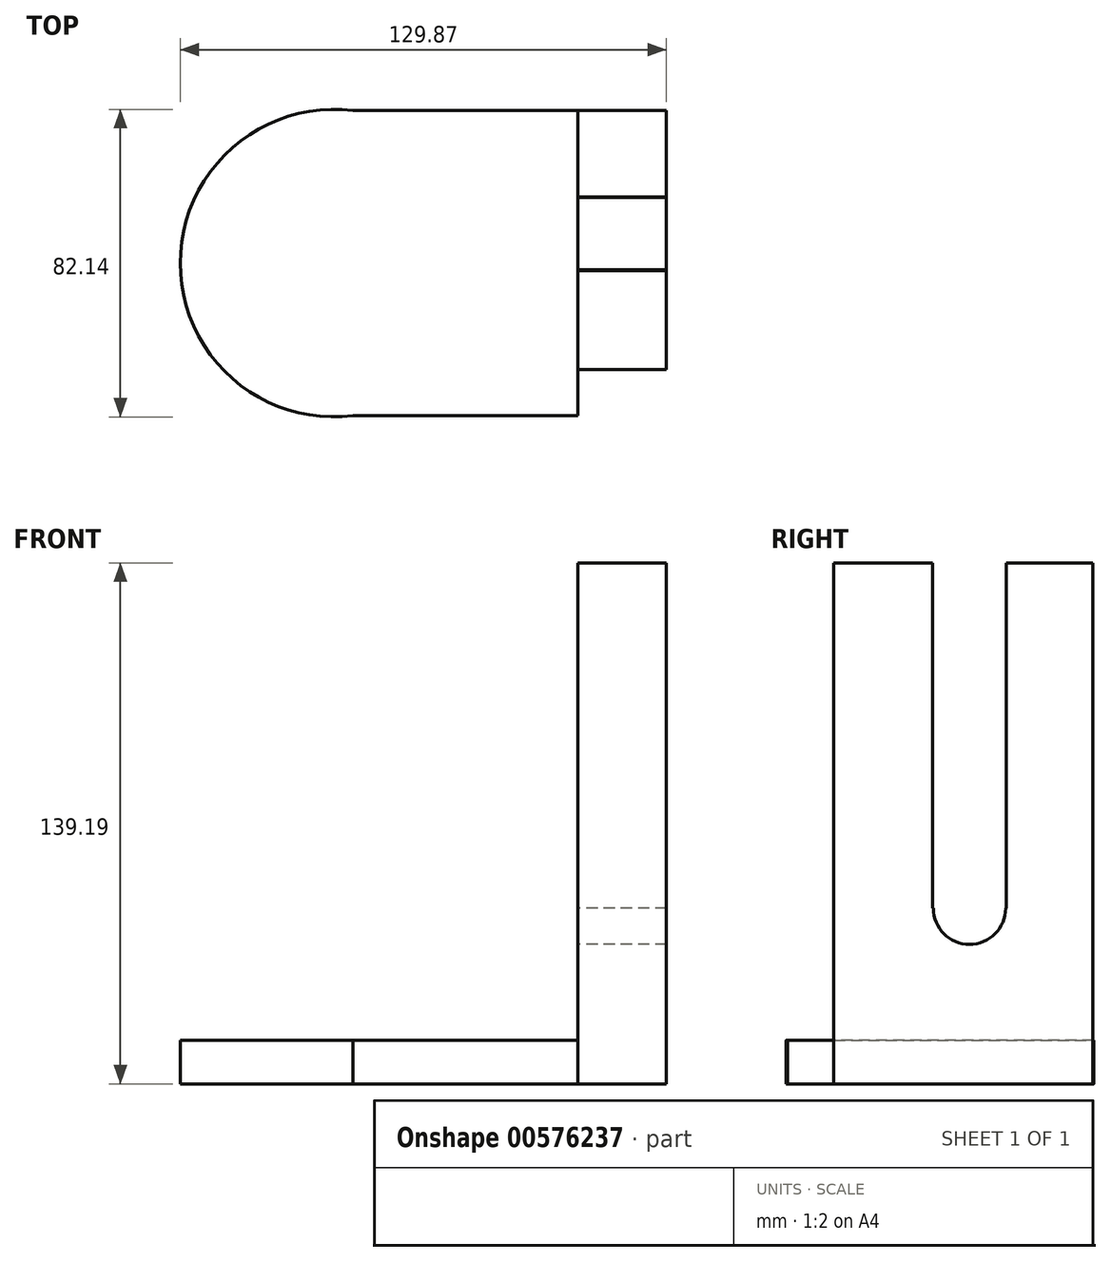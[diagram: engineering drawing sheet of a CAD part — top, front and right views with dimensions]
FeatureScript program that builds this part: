
annotation { "Feature Type Name" : "Feature", "Feature Type Description" : "" }
export const myFeature = defineFeature(function(context is Context, id is Id, definition is map)
    precondition{}
    {
        {
            var Q0;
            Q0=qCreatedBy(makeId("Top.planeOp"),FACE);
            var sketch = newSketch(context, id + "F0", { "sketchPlane" : qUnion([Q0])});
            skLineSegment(sketch, "E0.bottom", {"start": v(20.72, -40.75) * mm, "end": v(-44.4, -40.75) * mm});
            skLineSegment(sketch, "E0.top", {"start": v(44.4, 40.75) * mm, "end": v(-44.4, 40.75) * mm});
            skLineSegment(sketch, "E0.left", {"start": v(44.4, -28.37) * mm, "end": v(44.4, 40.75) * mm});
            skPoint(sketch, "E0.middle", {"position": v(0, 0) * mm});
            skArc(sketch, "E1", {"start": v(-39.3, 40.75) * mm, "mid": v(-85.47, 0) * mm, "end": v(-39.3, -40.75) * mm});
            skLineSegment(sketch, "E2.top", {"start": v(44.4, -28.37) * mm, "end": v(20.72, -28.37) * mm});
            skLineSegment(sketch, "E2.right", {"start": v(20.72, -40.75) * mm, "end": v(20.72, -28.37) * mm});
            skPoint(sketch, "E3.orphan", {"position": v(44.4, -40.75) * mm});
            skSolve(sketch);
        }
        {
            var Q0;
            {var subQ1=sQuery(id+"F0.wireOp",EDGE,"E0.left");Q0=makeQuery(id+"F0.imprint","IMPRINT",FACE,{"disambiguationData":[TD([[makeQuery(id+"F0.imprint","IMPRINT",EDGE,{"derivedFrom":subQ1}),1.0]])]});}
            var sketch = newSketch(context, id + "F1", { "sketchPlane" : qUnion([Q0])});
            skSolve(sketch);
        }
        {
            var Q0;
            Q0 = qSketchRegion(id + "F1", true);
            var Q1;
            {var subQ1=sQuery(id+"F0.wireOp",EDGE,"E0.left");Q1=makeQuery(id+"F0.imprint","IMPRINT",FACE,{"disambiguationData":[TD([[makeQuery(id+"F0.imprint","IMPRINT",EDGE,{"derivedFrom":subQ1}),1.0]])]});}
            extrude(context, id + "F2", {"entities" : qUnion([Q0, Q1]), "depth" : 11.68 * mm, "offsetDistance" : 25.4 * mm});
        }
        {
            var Q0;
            Q0=makeQuery(id+"F2.opExtrude","CAP_FACE",FACE,{"disambiguationData":[OSD([sQuery(id+"F0.wireOp",EDGE,"E0.bottom"),sQuery(id+"F0.wireOp",EDGE,"E0.top"),sQuery(id+"F0.wireOp",EDGE,"E0.left"),sQuery(id+"F0.wireOp",EDGE,"E1"),sQuery(id+"F0.wireOp",EDGE,"E2.top"),sQuery(id+"F0.wireOp",EDGE,"E2.right")])],"isStart":false});
            var sketch = newSketch(context, id + "F3", { "sketchPlane" : qUnion([Q0])});
            skLineSegment(sketch, "E4", {"start": v(20.72, -28.37) * mm, "end": v(20.72, 40.75) * mm});
            skSolve(sketch);
        }
        {
            var Q0;
            {var subQ0=sQuery(id+"F3.wireOp",EDGE,"E4");Q0=makeQuery(id+"F3.imprint","IMPRINT",FACE,{"disambiguationData":[TD([[makeQuery(id+"F3.imprint","IMPRINT",EDGE,{"derivedFrom":subQ0}),-1.0]])]});}
            extrude(context, id + "F4", {"entities" : qUnion([Q0]), "operationType" : NewBodyOperationType.ADD, "depth" : 25.4 * mm, "offsetDistance" : 25.4 * mm});
        }
        {
            var Q0;
            Q0=makeQuery(id+"F4.opExtrude","CAP_FACE",FACE,{"disambiguationData":[OSD([sQuery(id+"F0.wireOp",EDGE,"E0.top"),sQuery(id+"F0.wireOp",EDGE,"E0.left"),sQuery(id+"F0.wireOp",EDGE,"E2.top"),sQuery(id+"F3.wireOp",EDGE,"E4")])],"isStart":false});
            extrude(context, id + "F5", {"entities" : qUnion([Q0]), "operationType" : NewBodyOperationType.ADD, "depth" : 102.1 * mm, "offsetDistance" : 25.4 * mm});
        }
        {
            var Q0;
            {var subQ0=sQuery(id+"F3.wireOp",EDGE,"E4");Q0=makeQuery(id+"F5.boolean.opBoolean","MERGE",FACE,{"derivedFrom":[makeQuery(id+"F4.opExtrude","SWEPT_FACE",FACE,{"disambiguationData":[OSD([subQ0])]}),makeQuery(id+"F5.opExtrude","SWEPT_FACE",FACE,{"disambiguationData":[OSD([subQ0])]})]});}
            var sketch = newSketch(context, id + "F6", { "sketchPlane" : qUnion([Q0])});
            skLineSegment(sketch, "E5.bottom", {"start": v(-17.7, 139.2) * mm, "end": v(1.97, 139.2) * mm});
            skLineSegment(sketch, "E5.top", {"start": v(-17.7, 46.9) * mm, "end": v(-17.5, 46.9) * mm});
            skLineSegment(sketch, "E5.left", {"start": v(-17.7, 139.2) * mm, "end": v(-17.7, 46.9) * mm});
            skLineSegment(sketch, "E5.right", {"start": v(1.97, 139.2) * mm, "end": v(1.97, 46.9) * mm});
            skArc(sketch, "E6", {"start": v(-17.5, 46.9) * mm, "mid": v(-7.86, 37.26) * mm, "end": v(1.77, 46.9) * mm});
            skLineSegment(sketch, "E7.trimOffspring", {"start": v(1.77, 46.9) * mm, "end": v(1.97, 46.9) * mm});
            skSolve(sketch);
        }
        {
            var Q0;
            Q0 = qSketchRegion(id + "F6", true);
            extrude(context, id + "F7", {"entities" : qUnion([Q0]), "operationType" : NewBodyOperationType.ADD, "depth" : 25.4 * mm, "offsetDistance" : 25.4 * mm});
        }
        {
            var Q0;
            Q0=makeQuery(id+"F7.opExtrude","CAP_FACE",FACE,{"disambiguationData":[OSD([sQuery(id+"F6.wireOp",EDGE,"E5.bottom"),sQuery(id+"F6.wireOp",EDGE,"E5.top"),sQuery(id+"F6.wireOp",EDGE,"E5.left"),sQuery(id+"F6.wireOp",EDGE,"E5.right"),sQuery(id+"F6.wireOp",EDGE,"E6"),sQuery(id+"F6.wireOp",EDGE,"E7.trimOffspring")])],"isStart":false});
            extrude(context, id + "F8", {"entities" : qUnion([Q0]), "operationType" : NewBodyOperationType.REMOVE, "oppositeDirection" : true, "depth" : 110.49 * mm, "offsetDistance" : 25.4 * mm});
        }
    });
